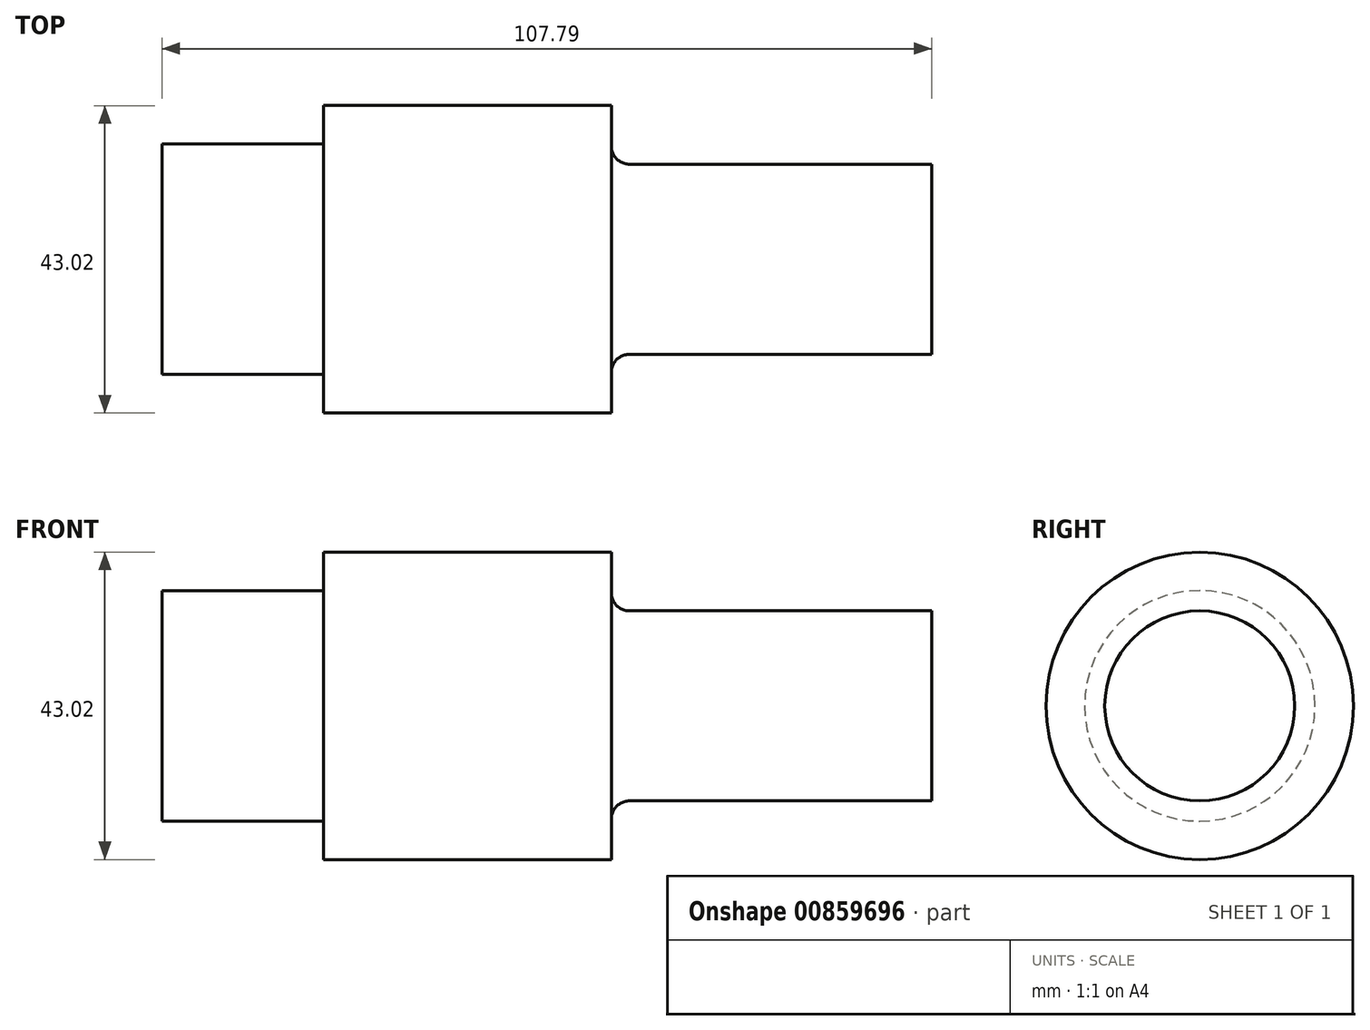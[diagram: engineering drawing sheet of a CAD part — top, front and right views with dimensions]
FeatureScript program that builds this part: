
annotation { "Feature Type Name" : "Feature", "Feature Type Description" : "" }
export const myFeature = defineFeature(function(context is Context, id is Id, definition is map)
    precondition{}
    {
        {
            var Q0;
            Q0=qCreatedBy(makeId("Front.planeOp"),FACE);
            var sketch = newSketch(context, id + "F0", { "sketchPlane" : qUnion([Q0])});
            skLineSegment(sketch, "E0", {"start": v(0, 0) * mm, "end": v(0, 16.14) * mm});
            skLineSegment(sketch, "E1", {"start": v(0, 16.14) * mm, "end": v(22.63, 16.14) * mm});
            skLineSegment(sketch, "E2", {"start": v(22.63, 16.14) * mm, "end": v(22.63, 21.51) * mm});
            skLineSegment(sketch, "E3", {"start": v(22.63, 21.51) * mm, "end": v(62.92, 21.51) * mm});
            skLineSegment(sketch, "E4", {"start": v(62.92, 21.51) * mm, "end": v(62.92, 13.3) * mm});
            skLineSegment(sketch, "E5", {"start": v(62.92, 13.3) * mm, "end": v(107.8, 13.3) * mm});
            skLineSegment(sketch, "E6", {"start": v(107.8, 13.3) * mm, "end": v(107.8, 0) * mm});
            skLineSegment(sketch, "E7", {"start": v(107.8, 0) * mm, "end": v(0, 0) * mm});
            skSolve(sketch);
        }
        {
            var Q0;
            Q0 = qSketchRegion(id + "F0", true);
            var Q1;
            Q1=sQuery(id+"F0.wireOp",EDGE,"E7");
            revolve(context, id + "F1", {"surfaceOperationType" : NewSurfaceOperationType.NEW, "entities" : qUnion([Q0]), "axis" : qUnion([Q1]), "revolveType" : RevolveType.FULL});
        }
        {
            var Q0;
            Q0=makeQuery(id+"F1.opRevolve","SWEPT_EDGE",EDGE,{"disambiguationData":[OSD([sQuery(id+"F0.wireOp",EDGE,"E4"),sQuery(id+"F0.wireOp",EDGE,"E5")])]});
            fillet(context, id + "F2", {"entities" : qUnion([Q0]), "radius" : 2.54 * mm, "tangentPropagation" : true, "allowEdgeOverflow" : false});
        }
    });
